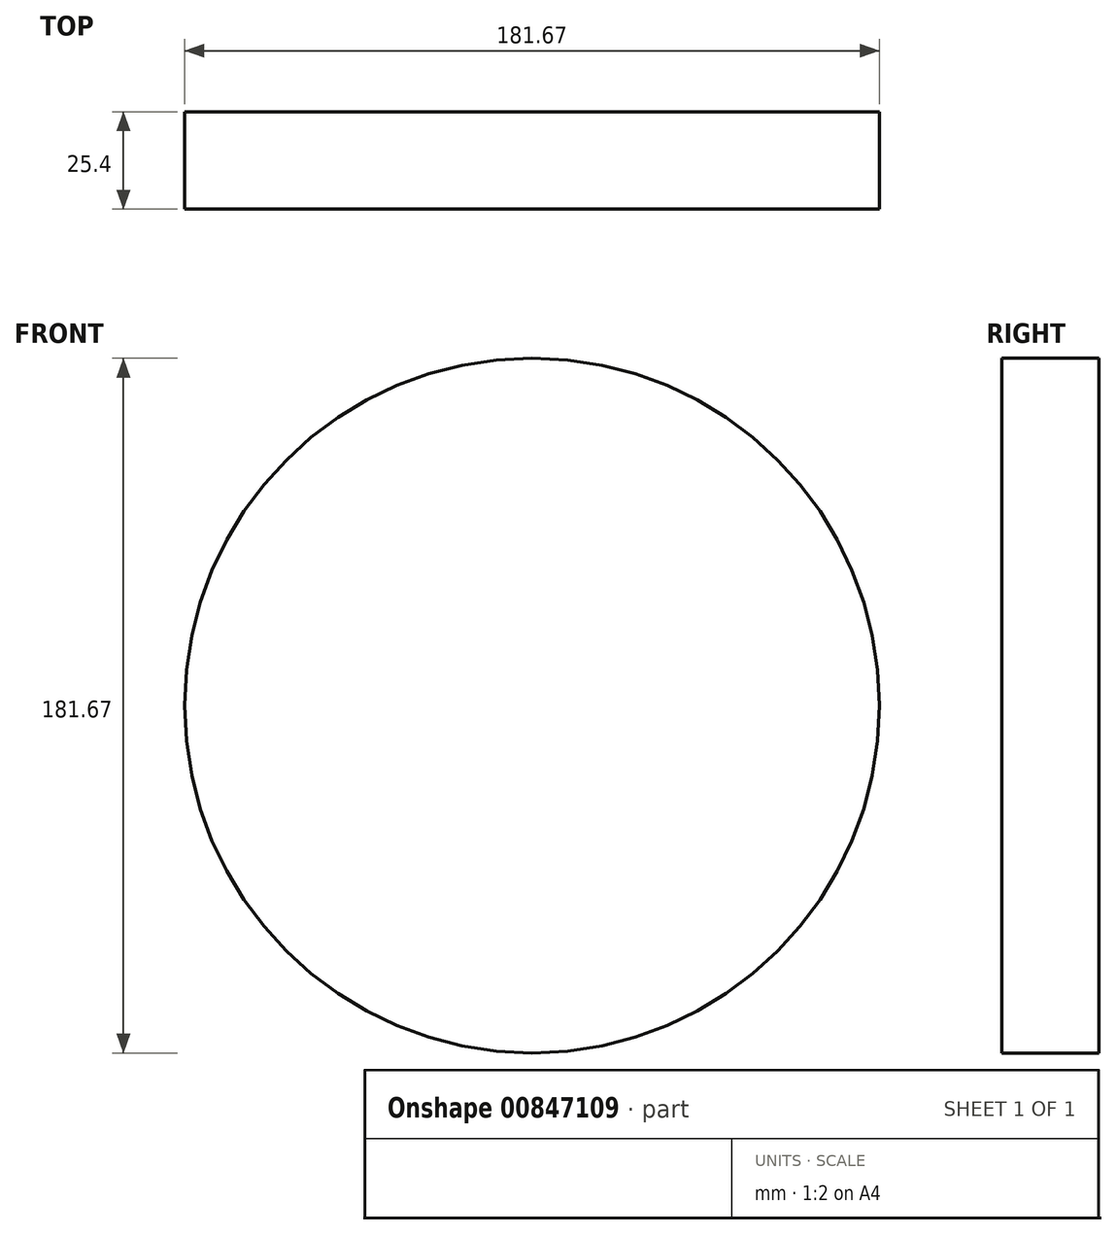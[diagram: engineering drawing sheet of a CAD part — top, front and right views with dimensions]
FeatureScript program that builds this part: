
annotation { "Feature Type Name" : "Feature", "Feature Type Description" : "" }
export const myFeature = defineFeature(function(context is Context, id is Id, definition is map)
    precondition{}
    {
        {
            var Q0;
            Q0=qCreatedBy(makeId("Front.planeOp"),FACE);
            var sketch = newSketch(context, id + "F0", { "sketchPlane" : qUnion([Q0])});
            skCircle(sketch, "E0", {"center": v(-60.53, 61.05) * mm, "radius": 90.84 * mm});
            skSolve(sketch);
        }
        {
            var Q0;
            Q0=makeQuery(id+"F0.imprint","IMPRINT",FACE,{"disambiguationData":[TD([[makeQuery(id+"F0.imprint","IMPRINT",EDGE,{"derivedFrom":sQuery(id+"F0.wireOp",EDGE,"E0")}),1.0]])]});
            extrude(context, id + "F1", {"entities" : qUnion([Q0]), "depth" : 25.4 * mm, "offsetDistance" : 25.4 * mm});
        }
    });
